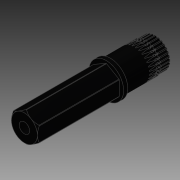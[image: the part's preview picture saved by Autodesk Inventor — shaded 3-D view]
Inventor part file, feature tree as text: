
AUTODESK INVENTOR PART (.ipt)
format: ipt  version: 2014 SP1 (Build 180222100, 222)  size: 2,135,552 bytes
history: native  units: in
note: dims shown in document units (in); Inventor stores cm internally (conversion verified against a paired STEP export)
features: fillet x1, imported_body x1
ambient origin geometry x8: Origin, YZ Plane, XZ Plane, XY Plane, X Axis, Y Axis, Z Axis, Center Point
bodies: Body1 (feature_tree)
feature tree (2):
  fillet  "Fillet5"  [1 undecoded]
  imported_body  "Base1"
note: 1 required parameter value undecoded (feature->parameter linkage not recoverable at this tier; creation-order binding heuristic only, values carry confidence <= 0.55)
